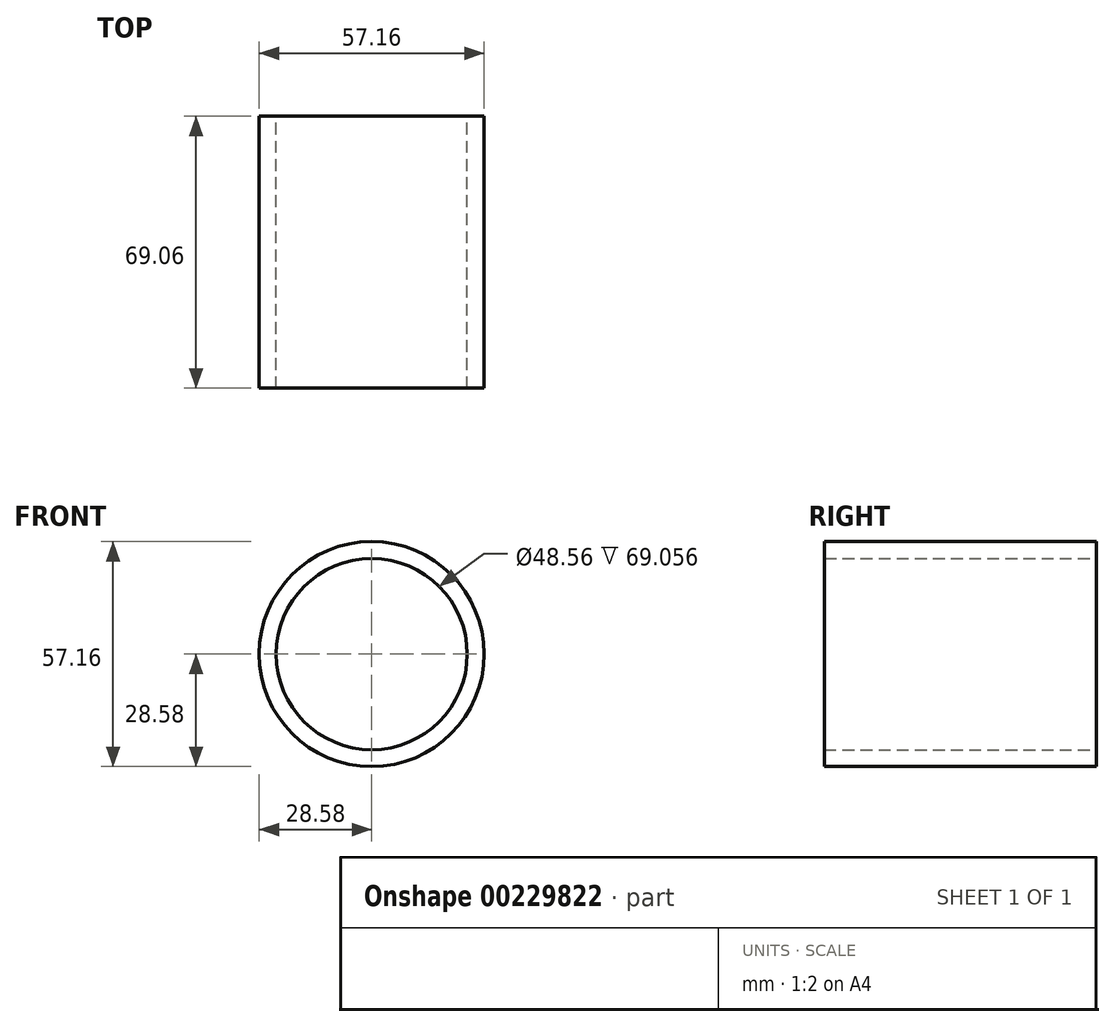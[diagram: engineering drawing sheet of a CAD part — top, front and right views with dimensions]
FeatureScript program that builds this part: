
annotation { "Feature Type Name" : "Feature", "Feature Type Description" : "" }
export const myFeature = defineFeature(function(context is Context, id is Id, definition is map)
    precondition{}
    {
        {
            var Q0;
            Q0=qCreatedBy(makeId("Front.planeOp"),FACE);
            var sketch = newSketch(context, id + "F0", { "sketchPlane" : qUnion([Q0])});
            skCircle(sketch, "E0", {"center": v(0, 0) * mm, "radius": 24.28 * mm});
            skCircle(sketch, "E1", {"center": v(0, 0) * mm, "radius": 28.58 * mm});
            skSolve(sketch);
        }
        {
            var Q0;
            Q0 = qSketchRegion(id + "F0", true);
            extrude(context, id + "F1", {"entities" : qUnion([Q0]), "depth" : 69.06 * mm});
        }
    });
